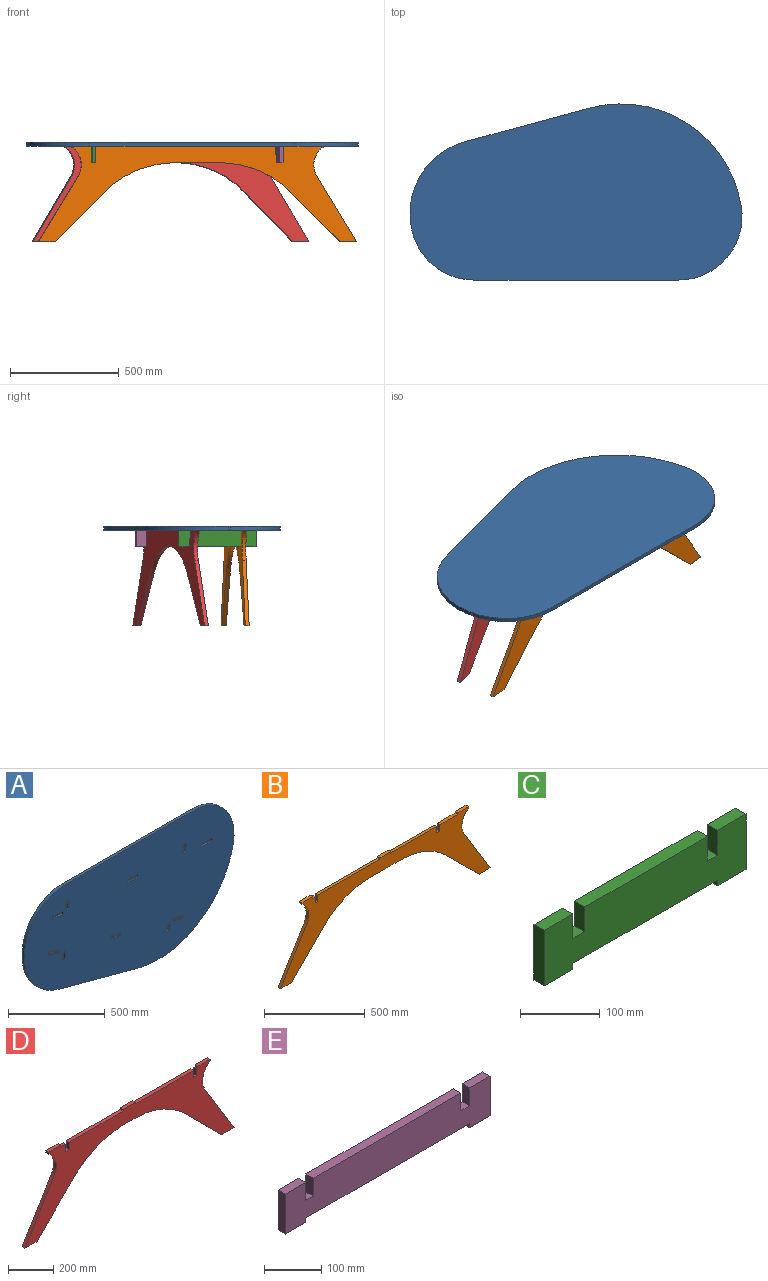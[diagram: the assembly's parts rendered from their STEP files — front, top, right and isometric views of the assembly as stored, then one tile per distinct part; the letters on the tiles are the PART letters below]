
ASSEMBLY  parts=5 mates=4
PART A: 60 faces, bbox 1529.5x18x811.4 mm
  f0: plane 943.12x18.03mm, normal (0,0,1), area 17008.3mm2, adj f1,f47,f48,f49
  f1: cylinder r=292.1mm len=285.54mm, axis (0,1,0), area 7155.9mm2, adj f0,f2,f48,f49
  f2: plane 18.03x4.92mm, normal (-0.98,0,0.21), area 90.7mm2, adj f1,f3,f48,f49
  f3: cylinder r=341.26mm len=401.41mm, axis (0,1,0), area 9353.1mm2, adj f2,f4,f48,f49
  f4: plane 575.7x155.23mm, normal (-0.26,0,-0.97), area 10753mm2, adj f3,f5,f48,f49
  f5: cylinder r=558.8mm len=696.61mm, axis (0,1,0), area 16812.7mm2, adj f4,f6,f48,f49
  f6: plane 18.03x4.48mm, normal (0.99,0,-0.17), area 81.9mm2, adj f5,f47,f48,f49
  f7: plane 17.45x9.02mm, normal (-0.25,0,-0.97), area 162.6mm2, adj f8,f37,f48,f53
  f8: plane 49.17x12.78mm, normal (-0.97,0,0.25), area 458.1mm2, adj f7,f9,f48,f53
  f9: plane 17.45x9.02mm, normal (0.25,0,0.97), area 162.6mm2, adj f8,f37,f48,f53
  f10: plane 49.17x12.78mm, normal (-0.97,0,0.25), area 458.1mm2, adj f11,f38,f48,f52
  f11: plane 17.45x9.02mm, normal (0.25,0,0.97), area 162.6mm2, adj f10,f12,f48,f52
  f12: plane 49.17x12.78mm, normal (0.97,0,-0.25), area 458.1mm2, adj f11,f38,f48,f52
  f13: plane 50.65x9.02mm, normal (1,0,-0.08), area 458.1mm2, adj f14,f39,f48,f51
  f14: plane 17.98x9.02mm, normal (-0.08,0,-1), area 162.6mm2, adj f13,f15,f48,f51
  f15: plane 50.65x9.02mm, normal (-1,0,0.08), area 458.1mm2, adj f14,f39,f48,f51
  f16: plane 75.98x9.02mm, normal (-0.08,0,-1), area 687.1mm2, adj f17,f40,f48,f57
  f17: plane 17.98x9.02mm, normal (-1,0,0.08), area 162.6mm2, adj f16,f18,f48,f57
  f18: plane 75.98x9.02mm, normal (0.08,0,1), area 687.1mm2, adj f17,f40,f48,f57
  f19: plane 17.45x9.02mm, normal (0.97,0,-0.25), area 162.6mm2, adj f20,f41,f48,f59
  f20: plane 73.75x19.17mm, normal (-0.25,0,-0.97), area 687.1mm2, adj f19,f21,f48,f59
  f21: plane 17.45x9.02mm, normal (-0.97,0,0.25), area 162.6mm2, adj f20,f41,f48,f59
  f22: plane 17.45x9.02mm, normal (0.97,0,-0.25), area 162.6mm2, adj f23,f42,f48,f58
  f23: plane 73.75x19.17mm, normal (-0.25,0,-0.97), area 687.1mm2, adj f22,f24,f48,f58
  f24: plane 17.45x9.02mm, normal (-0.97,0,0.25), area 162.6mm2, adj f23,f42,f48,f58
  f25: plane 17.98x9.02mm, normal (1,0,-0.08), area 162.6mm2, adj f26,f43,f48,f56
  f26: plane 75.98x9.02mm, normal (-0.08,0,-1), area 687.1mm2, adj f25,f27,f48,f56
  f27: plane 17.98x9.02mm, normal (-1,0,0.08), area 162.6mm2, adj f26,f43,f48,f56
  f28: plane 75.98x9.02mm, normal (0.08,0,1), area 687.1mm2, adj f29,f44,f48,f55
  f29: plane 17.98x9.02mm, normal (1,0,-0.08), area 162.6mm2, adj f28,f30,f48,f55
  f30: plane 75.98x9.02mm, normal (-0.08,0,-1), area 687.1mm2, adj f29,f44,f48,f55
  f31: plane 73.75x19.17mm, normal (0.25,0,0.97), area 687.1mm2, adj f32,f45,f48,f54
  f32: plane 17.45x9.02mm, normal (0.97,0,-0.25), area 162.6mm2, adj f31,f33,f48,f54
  f33: plane 73.75x19.17mm, normal (-0.25,0,-0.97), area 687.1mm2, adj f32,f45,f48,f54
  f34: plane 50.65x9.02mm, normal (1,0,-0.08), area 458.1mm2, adj f35,f46,f48,f50
  f35: plane 17.98x9.02mm, normal (-0.08,0,-1), area 162.6mm2, adj f34,f36,f48,f50
  f36: plane 50.65x9.02mm, normal (-1,0,0.08), area 458.1mm2, adj f35,f46,f48,f50
  f37: plane 49.17x12.78mm, normal (0.97,0,-0.25), area 458.1mm2, adj f7,f9,f48,f53
  f38: plane 17.45x9.02mm, normal (-0.25,0,-0.97), area 162.6mm2, adj f10,f12,f48,f52
  f39: plane 17.98x9.02mm, normal (0.08,0,1), area 162.6mm2, adj f13,f15,f48,f51
  f40: plane 17.98x9.02mm, normal (1,0,-0.08), area 162.6mm2, adj f16,f18,f48,f57
  f41: plane 73.75x19.17mm, normal (0.25,0,0.97), area 687.1mm2, adj f19,f21,f48,f59
  f42: plane 73.75x19.17mm, normal (0.25,0,0.97), area 687.1mm2, adj f22,f24,f48,f58
  f43: plane 75.98x9.02mm, normal (0.08,0,1), area 687.1mm2, adj f25,f27,f48,f56
  f44: plane 17.98x9.02mm, normal (-1,0,0.08), area 162.6mm2, adj f28,f30,f48,f55
  f45: plane 17.45x9.02mm, normal (-0.97,0,0.25), area 162.6mm2, adj f31,f33,f48,f54
  f46: plane 17.98x9.02mm, normal (0.08,0,1), area 162.6mm2, adj f34,f36,f48,f50
  f47: cylinder r=292.1mm len=340.31mm, axis (0,1,0), area 9148mm2, adj f0,f6,f48,f49
  f48: plane 1529.49x811.36mm, normal (0,-1,0), area 1003923.4mm2, adj f0,f1,f2,f3,f4,f5,f6,f7
  f49: plane 1529.49x811.36mm, normal (0,1,0), area 1015833.1mm2, adj f0,f1,f2,f3,f4,f5,f6,f47
  f50: plane 52.03x21.85mm, normal (0,-1,0), area 916.1mm2, adj f34,f35,f36,f46
  f51: plane 52.03x21.85mm, normal (0,-1,0), area 916.1mm2, adj f13,f14,f15,f39
  f52: plane 53.7x30.24mm, normal (0,-1,0), area 916.1mm2, adj f10,f11,f12,f38
  f53: plane 53.7x30.24mm, normal (0,-1,0), area 916.1mm2, adj f7,f8,f9,f37
  f54: plane 78.29x36.63mm, normal (0,-1,0), area 1374.2mm2, adj f31,f32,f33,f45
  f55: plane 77.35x23.78mm, normal (0,-1,0), area 1374.2mm2, adj f28,f29,f30,f44
  f56: plane 77.35x23.78mm, normal (0,-1,0), area 1374.2mm2, adj f25,f26,f27,f43
  f57: plane 77.35x23.78mm, normal (0,-1,0), area 1374.2mm2, adj f16,f17,f18,f40
  f58: plane 78.29x36.63mm, normal (0,-1,0), area 1374.2mm2, adj f22,f23,f24,f42
  f59: plane 78.29x36.63mm, normal (0,-1,0), area 1374.2mm2, adj f19,f20,f21,f41
PART B: 32 faces, bbox 1468.3x18x447.2 mm
  f0: plane 435.3x18.03mm, normal (0,0,1), area 7850.2mm2, adj f1,f29,f30,f31
  f1: plane 38.1x18.03mm, normal (-1,0,0), area 687.1mm2, adj f0,f2,f30,f31
  f2: plane 18.03x18.03mm, normal (0,0,1), area 325.2mm2, adj f1,f3,f30,f31
  f3: plane 38.1x18.03mm, normal (1,0,0), area 687.1mm2, adj f2,f4,f30,f31
  f4: plane 18.03x16.67mm, normal (0,0,1), area 300.6mm2, adj f3,f5,f30,f31
  f5: plane 18.03x9.02mm, normal (1,0,0), area 162.6mm2, adj f4,f6,f30,f31
  f6: plane 76.2x18.03mm, normal (0,0,1), area 1374.2mm2, adj f5,f7,f30,f31
  f7: plane 18.03x9.02mm, normal (-1,0,0), area 162.6mm2, adj f6,f8,f30,f31
  f8: cylinder r=101.38mm len=138.59mm, axis (0,1,0), area 2846.8mm2, adj f7,f9,f30,f31
  f9: plane 299.56x182.51mm, normal (-0.85,0,0.52), area 6325.9mm2, adj f8,f10,f30,f31
  f10: plane 76.2x18.03mm, normal (0,0,-1), area 1374.2mm2, adj f9,f11,f30,f31
  f11: plane 227.78x227.34mm, normal (0.71,0,-0.71), area 5803.7mm2, adj f10,f12,f30,f31
  f12: cylinder r=458.45mm len=304.89mm, axis (0,1,0), area 6147.9mm2, adj f11,f13,f30,f31
  f13: plane 251.46x18.03mm, normal (0,0,-1), area 4534.8mm2, adj f12,f14,f30,f31
  f14: cylinder r=458.45mm len=304.89mm, axis (0,1,0), area 6147.9mm2, adj f13,f15,f30,f31
  f15: plane 227.78x227.34mm, normal (-0.71,0,-0.71), area 5803.7mm2, adj f14,f16,f30,f31
  f16: plane 76.2x18.03mm, normal (0,0,-1), area 1374.2mm2, adj f15,f17,f30,f31
  f17: plane 299.56x182.51mm, normal (0.85,0,0.52), area 6325.9mm2, adj f16,f18,f30,f31
  f18: cylinder r=101.38mm len=138.59mm, axis (0,1,0), area 2846.8mm2, adj f17,f19,f30,f31
  f19: plane 18.03x9.02mm, normal (1,0,0), area 162.6mm2, adj f18,f20,f30,f31
  f20: plane 76.2x18.03mm, normal (0,0,1), area 1374.2mm2, adj f19,f21,f30,f31
  f21: plane 18.03x9.02mm, normal (-1,0,0), area 162.6mm2, adj f20,f22,f30,f31
  f22: plane 125.6x18.03mm, normal (0,0,1), area 2265.1mm2, adj f21,f23,f30,f31
  f23: plane 38.1x18.03mm, normal (-1,0,0), area 687.1mm2, adj f22,f24,f30,f31
  f24: plane 21.57x18.03mm, normal (0,0,1), area 389mm2, adj f23,f25,f30,f31
  f25: plane 38.1x18.03mm, normal (1,0,0), area 687.1mm2, adj f24,f26,f30,f31
  f26: plane 322.82x18.03mm, normal (0,0,1), area 5821.8mm2, adj f25,f27,f30,f31
  f27: plane 18.03x9.02mm, normal (1,0,0), area 162.6mm2, adj f26,f28,f30,f31
  f28: plane 76.2x18.03mm, normal (0,0,1), area 1374.2mm2, adj f27,f29,f30,f31
  f29: plane 18.03x9.02mm, normal (-1,0,0), area 162.6mm2, adj f0,f28,f30,f31
  f30: plane 1468.32x447.17mm, normal (0,-1,0), area 200822.8mm2, adj f0,f1,f2,f3,f4,f5,f6,f7
  f31: plane 1468.32x447.17mm, normal (0,1,0), area 200822.8mm2, adj f0,f1,f2,f3,f4,f5,f6,f7
PART C: 18 faces, bbox 358.2x18x85.2 mm
  f0: plane 256.62x18.03mm, normal (0,0,-1), area 4627.8mm2, adj f1,f15,f16,f17
  f1: plane 18.03x9.02mm, normal (-1,0,0), area 162.6mm2, adj f0,f2,f16,f17
  f2: plane 50.8x18.03mm, normal (0,0,-1), area 916.1mm2, adj f1,f3,f16,f17
  f3: plane 85.22x18.03mm, normal (1,0,0), area 1536.8mm2, adj f2,f4,f16,f17
  f4: plane 50.8x18.03mm, normal (0,0,1), area 916.1mm2, adj f3,f5,f16,f17
  f5: plane 38.1x18.03mm, normal (-1,0,0), area 687.1mm2, adj f4,f6,f16,f17
  f6: plane 18.03x18.03mm, normal (0,0,1), area 325.2mm2, adj f5,f7,f16,f17
  f7: plane 38.1x18.03mm, normal (1,0,0), area 687.1mm2, adj f6,f8,f16,f17
  f8: plane 217.01x18.03mm, normal (0,0,1), area 3913.6mm2, adj f7,f9,f16,f17
  f9: plane 38.1x18.03mm, normal (-1,0,0), area 687.1mm2, adj f8,f10,f16,f17
  f10: plane 21.57x18.03mm, normal (0,0,1), area 389mm2, adj f9,f11,f16,f17
  f11: plane 38.1x18.03mm, normal (1,0,0), area 687.1mm2, adj f10,f12,f16,f17
  f12: plane 50.8x18.03mm, normal (0,0,1), area 916.1mm2, adj f11,f13,f16,f17
  f13: plane 85.22x18.03mm, normal (-1,0,0), area 1536.8mm2, adj f12,f14,f16,f17
  f14: plane 50.8x18.03mm, normal (0,0,-1), area 916.1mm2, adj f13,f15,f16,f17
  f15: plane 18.03x9.02mm, normal (1,0,0), area 162.6mm2, adj f0,f14,f16,f17
  f16: plane 358.22x85.22mm, normal (0,-1,0), area 26703.3mm2, adj f0,f1,f2,f3,f4,f5,f6,f7
  f17: plane 358.22x85.22mm, normal (0,1,0), area 26703.3mm2, adj f0,f1,f2,f3,f4,f5,f6,f7
PART D: 32 faces, bbox 1312.2x18x447.2 mm
  f0: plane 364.01x18.03mm, normal (0,0,1), area 6564.6mm2, adj f1,f29,f30,f31
  f1: plane 18.03x9.02mm, normal (1,0,0), area 162.6mm2, adj f0,f2,f30,f31
  f2: plane 76.2x18.03mm, normal (0,0,1), area 1374.2mm2, adj f1,f3,f30,f31
  f3: plane 18.03x9.02mm, normal (-1,0,0), area 162.6mm2, adj f2,f4,f30,f31
  f4: plane 338.61x18.03mm, normal (0,0,1), area 6106.5mm2, adj f3,f5,f30,f31
  f5: plane 38.1x18.03mm, normal (-1,0,0), area 687.1mm2, adj f4,f6,f30,f31
  f6: plane 21.57x18.03mm, normal (0,0,1), area 389mm2, adj f5,f7,f30,f31
  f7: plane 38.1x18.03mm, normal (1,0,0), area 687.1mm2, adj f6,f8,f30,f31
  f8: plane 31.77x18.03mm, normal (0,0,1), area 572.9mm2, adj f7,f9,f30,f31
  f9: plane 18.03x9.02mm, normal (1,0,0), area 162.6mm2, adj f8,f10,f30,f31
  f10: plane 76.2x18.03mm, normal (0,0,1), area 1374.2mm2, adj f9,f11,f30,f31
  f11: plane 18.03x9.02mm, normal (-1,0,0), area 162.6mm2, adj f10,f12,f30,f31
  f12: cylinder r=101.38mm len=138.59mm, axis (0,1,0), area 2846.8mm2, adj f11,f13,f30,f31
  f13: plane 299.56x182.51mm, normal (-0.85,0,0.52), area 6325.9mm2, adj f12,f14,f30,f31
  f14: plane 76.2x18.03mm, normal (0,0,-1), area 1374.2mm2, adj f13,f15,f30,f31
  f15: plane 227.78x227.34mm, normal (0.71,0,-0.71), area 5803.7mm2, adj f14,f16,f30,f31
  f16: cylinder r=458.45mm len=304.89mm, axis (0,1,0), area 6147.9mm2, adj f15,f17,f30,f31
  f17: plane 95.37x18.03mm, normal (0,0,-1), area 1719.9mm2, adj f16,f18,f30,f31
  f18: cylinder r=458.45mm len=304.89mm, axis (0,1,0), area 6147.9mm2, adj f17,f19,f30,f31
  f19: plane 227.78x227.34mm, normal (-0.71,0,-0.71), area 5803.7mm2, adj f18,f20,f30,f31
  f20: plane 76.2x18.03mm, normal (0,0,-1), area 1374.2mm2, adj f19,f21,f30,f31
  f21: plane 299.56x182.51mm, normal (0.85,0,0.52), area 6325.9mm2, adj f20,f22,f30,f31
  f22: cylinder r=101.38mm len=138.59mm, axis (0,1,0), area 2846.8mm2, adj f21,f23,f30,f31
  f23: plane 18.03x9.02mm, normal (1,0,0), area 162.6mm2, adj f22,f24,f30,f31
  f24: plane 76.2x18.03mm, normal (0,0,1), area 1374.2mm2, adj f23,f25,f30,f31
  f25: plane 18.03x9.02mm, normal (-1,0,0), area 162.6mm2, adj f24,f26,f30,f31
  f26: plane 18.03x9.91mm, normal (0,0,1), area 178.6mm2, adj f25,f27,f30,f31
  f27: plane 38.1x18.03mm, normal (-1,0,0), area 687.1mm2, adj f26,f28,f30,f31
  f28: plane 18.03x18.03mm, normal (0,0,1), area 325.2mm2, adj f27,f29,f30,f31
  f29: plane 38.1x18.03mm, normal (1,0,0), area 687.1mm2, adj f0,f28,f30,f31
  f30: plane 1312.22x447.17mm, normal (0,-1,0), area 188928.6mm2, adj f0,f1,f2,f3,f4,f5,f6,f7
  f31: plane 1312.22x447.17mm, normal (0,1,0), area 188928.6mm2, adj f0,f1,f2,f3,f4,f5,f6,f7
PART E: 18 faces, bbox 505.9x18x85.2 mm
  f0: plane 404.25x18.03mm, normal (0,0,-1), area 7290.3mm2, adj f1,f15,f16,f17
  f1: plane 18.03x9.02mm, normal (-1,0,0), area 162.6mm2, adj f0,f2,f16,f17
  f2: plane 50.8x18.03mm, normal (0,0,-1), area 916.1mm2, adj f1,f3,f16,f17
  f3: plane 85.22x18.03mm, normal (1,0,0), area 1536.8mm2, adj f2,f4,f16,f17
  f4: plane 50.8x18.03mm, normal (0,0,1), area 916.1mm2, adj f3,f5,f16,f17
  f5: plane 38.1x18.03mm, normal (-1,0,0), area 687.1mm2, adj f4,f6,f16,f17
  f6: plane 21.57x18.03mm, normal (0,0,1), area 389mm2, adj f5,f7,f16,f17
  f7: plane 38.1x18.03mm, normal (1,0,0), area 687.1mm2, adj f6,f8,f16,f17
  f8: plane 364.65x18.03mm, normal (0,0,1), area 6576mm2, adj f7,f9,f16,f17
  f9: plane 38.1x18.03mm, normal (-1,0,0), area 687.1mm2, adj f8,f10,f16,f17
  f10: plane 18.03x18.03mm, normal (0,0,1), area 325.2mm2, adj f9,f11,f16,f17
  f11: plane 38.1x18.03mm, normal (1,0,0), area 687.1mm2, adj f10,f12,f16,f17
  f12: plane 50.8x18.03mm, normal (0,0,1), area 916.1mm2, adj f11,f13,f16,f17
  f13: plane 85.22x18.03mm, normal (-1,0,0), area 1536.8mm2, adj f12,f14,f16,f17
  f14: plane 50.8x18.03mm, normal (0,0,-1), area 916.1mm2, adj f13,f15,f16,f17
  f15: plane 18.03x9.02mm, normal (1,0,0), area 162.6mm2, adj f0,f14,f16,f17
  f16: plane 505.85x85.22mm, normal (0,-1,0), area 37953mm2, adj f0,f1,f2,f3,f4,f5,f6,f7
  f17: plane 505.85x85.22mm, normal (0,1,0), area 37953mm2, adj f0,f1,f2,f3,f4,f5,f6,f7
PLACE A rot(axis=(1,0,0),90deg) t=(-235.07,-470.93,370.17)mm fixed
PLACE B rot(axis=(0,0,1),4.4deg) t=(-236.44,-310.71,1660.23)mm
PLACE C rot(axis=(-0.73,0.68,0),180deg) t=(-16.44,-3.69,-486.07)mm
PLACE D rot(axis=(0,0,1),14.6deg) t=(1054.16,219.7,1660.23)mm
PLACE E rot(axis=(-0.79,0.61,0),180deg) t=(746.39,192.17,-638.47)mm
MATE fastened C.f16 <-> A.f36  axis (1,0.08,0) through (26.87,-334.17,361.15)mm
MATE fastened A.f10 <-> E.f16  axis (-0.97,-0.25,0) through (884.74,-268.28,361.15)mm
MATE fastened A.f28 <-> B.f31  axis (0.08,-1,0) through (495.59,-254.83,361.15)mm
MATE fastened D.f31 <-> A.f31  axis (-0.25,0.97,0) through (370,41.82,361.15)mm
